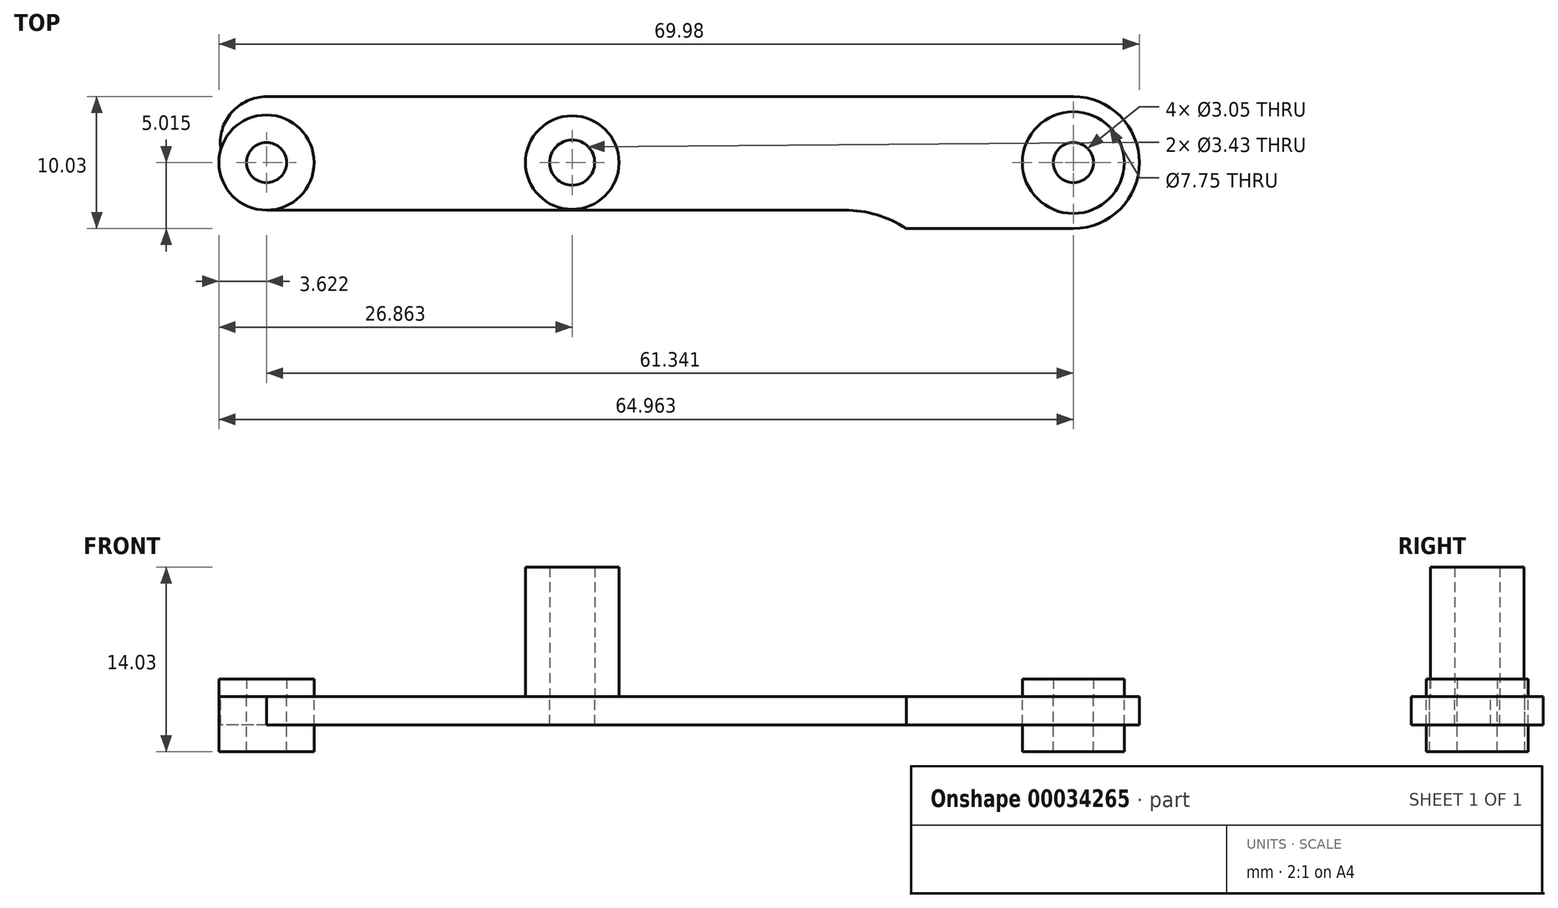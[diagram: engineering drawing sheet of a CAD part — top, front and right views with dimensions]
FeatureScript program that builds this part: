
annotation { "Feature Type Name" : "Feature", "Feature Type Description" : "" }
export const myFeature = defineFeature(function(context is Context, id is Id, definition is map)
    precondition{}
    {
        {
            var Q0;
            Q0=qCreatedBy(makeId("Top.planeOp"),FACE);
            var sketch = newSketch(context, id + "F0", { "sketchPlane" : qUnion([Q0])});
            skLineSegment(sketch, "E0", {"start": v(-0.05, 0.1) * mm, "end": v(23.2, 0.1) * mm, "construction": true});
            skLineSegment(sketch, "E1", {"start": v(23.2, 0.1) * mm, "end": v(61.3, 0.1) * mm, "construction": true});
            skCircle(sketch, "E2", {"center": v(-0.05, 0.1) * mm, "radius": 3.62 * mm});
            skCircle(sketch, "E3", {"center": v(23.2, 0.1) * mm, "radius": 3.56 * mm});
            skCircle(sketch, "E4", {"center": v(61.3, 0.1) * mm, "radius": 3.87 * mm});
            skCircle(sketch, "E5", {"center": v(61.3, 0.1) * mm, "radius": 1.52 * mm});
            skCircle(sketch, "E6", {"center": v(23.2, 0.1) * mm, "radius": 1.71 * mm});
            skCircle(sketch, "E7", {"center": v(-0.05, 0.1) * mm, "radius": 1.52 * mm});
            skLineSegment(sketch, "E8", {"start": v(-0.05, 5.11) * mm, "end": v(61.3, 5.11) * mm});
            skLineSegment(sketch, "E9", {"start": v(61.3, -4.92) * mm, "end": v(48.6, -4.92) * mm});
            skArc(sketch, "E10", {"start": v(48.6, -4.92) * mm, "mid": v(46.35, -3.88) * mm, "end": v(43.9, -3.52) * mm});
            skLineSegment(sketch, "E11", {"start": v(43.9, -3.52) * mm, "end": v(-0.05, -3.52) * mm});
            skCircle(sketch, "E12", {"center": v(61.3, 0.1) * mm, "radius": 5.02 * mm});
            skLineSegment(sketch, "E13", {"start": v(-0.05, 5.11) * mm, "end": v(-0.05, -3.52) * mm, "construction": true});
            skArc(sketch, "E14", {"start": v(-0.05, 5.11) * mm, "mid": v(-2.7, 3.9) * mm, "end": v(-3.53, 1.1) * mm});
            skSolve(sketch);
        }
        {
            var Q0;
            Q0=makeQuery(id+"F0.imprint","IMPRINT",FACE,{"disambiguationData":[TD([[makeQuery(id+"F0.imprint","IMPRINT",EDGE,{"derivedFrom":sQuery(id+"F0.wireOp",EDGE,"E2")}),1.0]])]});
            var Q1;
            Q1=makeQuery(id+"F0.imprint","IMPRINT",FACE,{"disambiguationData":[TD([[makeQuery(id+"F0.imprint","IMPRINT",EDGE,{"derivedFrom":sQuery(id+"F0.wireOp",EDGE,"E4")}),1.0]])]});
            extrude(context, id + "F1", {"entities" : qUnion([Q0, Q1]), "depth" : 1.35 * mm});
        }
        {
            var Q0;
            Q0=makeQuery(id+"F0.imprint","IMPRINT",FACE,{"disambiguationData":[TD([[makeQuery(id+"F0.imprint","IMPRINT",EDGE,{"derivedFrom":sQuery(id+"F0.wireOp",EDGE,"E3")}),1.0]])]});
            extrude(context, id + "F2", {"entities" : qUnion([Q0]), "depth" : 9.84 * mm});
        }
        {
            var Q0;
            Q0=makeQuery(id+"F0.imprint","IMPRINT",FACE,{"disambiguationData":[TD([[makeQuery(id+"F0.imprint","IMPRINT",EDGE,{"derivedFrom":sQuery(id+"F0.wireOp",EDGE,"E2")}),1.0]])]});
            var Q1;
            Q1=makeQuery(id+"F0.imprint","IMPRINT",FACE,{"disambiguationData":[TD([[makeQuery(id+"F0.imprint","IMPRINT",EDGE,{"derivedFrom":sQuery(id+"F0.wireOp",EDGE,"E4")}),1.0]])]});
            extrude(context, id + "F3", {"entities" : qUnion([Q0, Q1]), "oppositeDirection" : true, "depth" : 4.2 * mm});
        }
        {
            var Q0;
            Q0=makeQuery(id+"F0.imprint","IMPRINT",FACE,{"disambiguationData":[TD([[makeQuery(id+"F0.imprint","IMPRINT",EDGE,{"derivedFrom":sQuery(id+"F0.wireOp",EDGE,"E3")}),-1.0]])]});
            var Q1;
            Q1=makeQuery(id+"F0.imprint","IMPRINT",FACE,{"disambiguationData":[TD([[makeQuery(id+"F0.imprint","IMPRINT",EDGE,{"derivedFrom":sQuery(id+"F0.wireOp",EDGE,"E3")}),1.0]])]});
            var Q2;
            Q2=makeQuery(id+"F0.imprint","IMPRINT",FACE,{"disambiguationData":[TD([[makeQuery(id+"F0.imprint","IMPRINT",EDGE,{"derivedFrom":sQuery(id+"F0.wireOp",EDGE,"E4")}),-1.0]])]});
            extrude(context, id + "F4", {"entities" : qUnion([Q0, Q1, Q2]), "oppositeDirection" : true, "depth" : 2.16 * mm});
        }
    });
